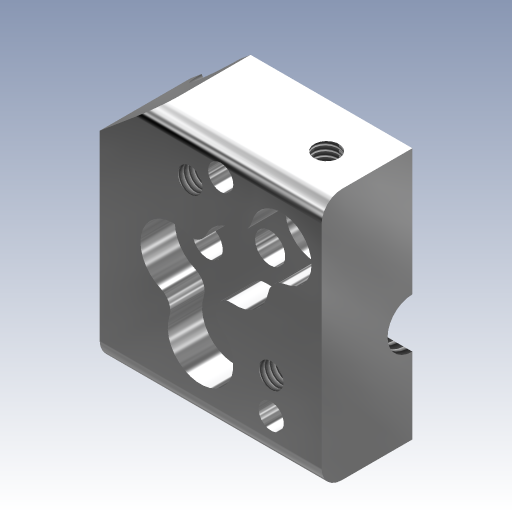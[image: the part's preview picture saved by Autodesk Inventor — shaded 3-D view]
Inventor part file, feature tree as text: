
AUTODESK INVENTOR PART (.ipt)
format: ipt  version: 2023.3 (Build 273359000, 359)  size: 416,768 bytes
history: native  units: mm (DEFAULTED — no unit token found)
features: other x10, sketch x8, hole x2, fillet x2, extrude x1
ambient origin geometry x1: Ursprung
bodies: Volumenkörper4 (feature_tree)
feature tree (23):
  other  "BT001_huenin20_23_Fiberprinter-Hotend_Heizblock_Seite1.ipt"
  sketch  "Skizze7"  dims[d1=3.0mm d2=10.0mm d3=6.5mm d4=3.4mm d5=90.0deg d6=8.0mm d7=20.594885mm d8=2.0mm d9=3.5mm]
  hole  "Bohrung1"  [1 undecoded]
  fillet  "Rundung1"  Radius=3.5mm
  hole  "Bohrung2"  [1 undecoded]
  extrude  "Extrusion1"  Depth=0.8mm
  fillet  "Rundung2"  Radius=0.8mm
  other  "YZ-Ebene"
  other  "XZ-Ebene"
  other  "XY-Ebene"
  other  "X-Achse"
  other  "Y-Achse"
  other  "Z-Achse"
  other  "Mittelpunkt"
  sketch  "Skizze3"  dims[d0=10.0mm]
  sketch  "Skizze19"  dims[d23=10.0mm d24=0.0mm]
  sketch  "Skizze20"  dims[d25=1.55mm]
  sketch  "Skizze21"  dims[d26=1.0mm]
  sketch  "Skizze22"  dims[d27=1.0mm d28=1.0mm d29=0.15mm d30=0.25mm d31=0.375mm d32=14.3117mm d33=0.75mm d34=20.594885mm d35=0.0625mm d36=0.75mm d37=0.375mm]
  other  "Volumenkörper4::BT001_huenin20_23_Fiberprinter-Hotend_Heizblock_Seite1.ipt"
  other  "Bezeichnung2"
  sketch  "Skizze8"  dims[d10=3.5mm d11=60.0deg]
  sketch  "Skizze9"  dims[d12=2.459mm d13=4.5mm d14=4.0mm d15=2.0mm d16=90.0deg d17=5.0mm d18=0.0mm d19=0.8mm d20=0.8mm d22=0.8mm]
note: 2 required parameter values undecoded (feature->parameter linkage not recoverable at this tier; creation-order binding heuristic only, values carry confidence <= 0.55)
